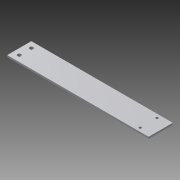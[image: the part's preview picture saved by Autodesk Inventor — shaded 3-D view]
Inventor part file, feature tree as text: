
AUTODESK INVENTOR PART (.ipt)
format: ipt  version: 2015 (Build 190159000, 159)  size: 117,760 bytes
history: native  units: mm
features: sketch x4, extrude x2, hole x2, other x1
ambient origin geometry x8: Origin, YZ Plane, XZ Plane, XY Plane, X Axis, Y Axis, Z Axis, Center Point
bodies: Body1 (feature_tree)
feature tree (9):
  other  "ソリッド1"
  extrude  "押し出し1"  Depth=112.0mm
  hole  "穴1"  [1 undecoded]
  hole  "穴3"  [1 undecoded]
  extrude  "押し出し3"  Depth=10.0mm
  sketch  "スケッチ1"
  sketch  "スケッチ3"
  sketch  "スケッチ5"
  sketch  "スケッチ6"
note: 2 required parameter values undecoded (feature->parameter linkage not recoverable at this tier; creation-order binding heuristic only, values carry confidence <= 0.55)
